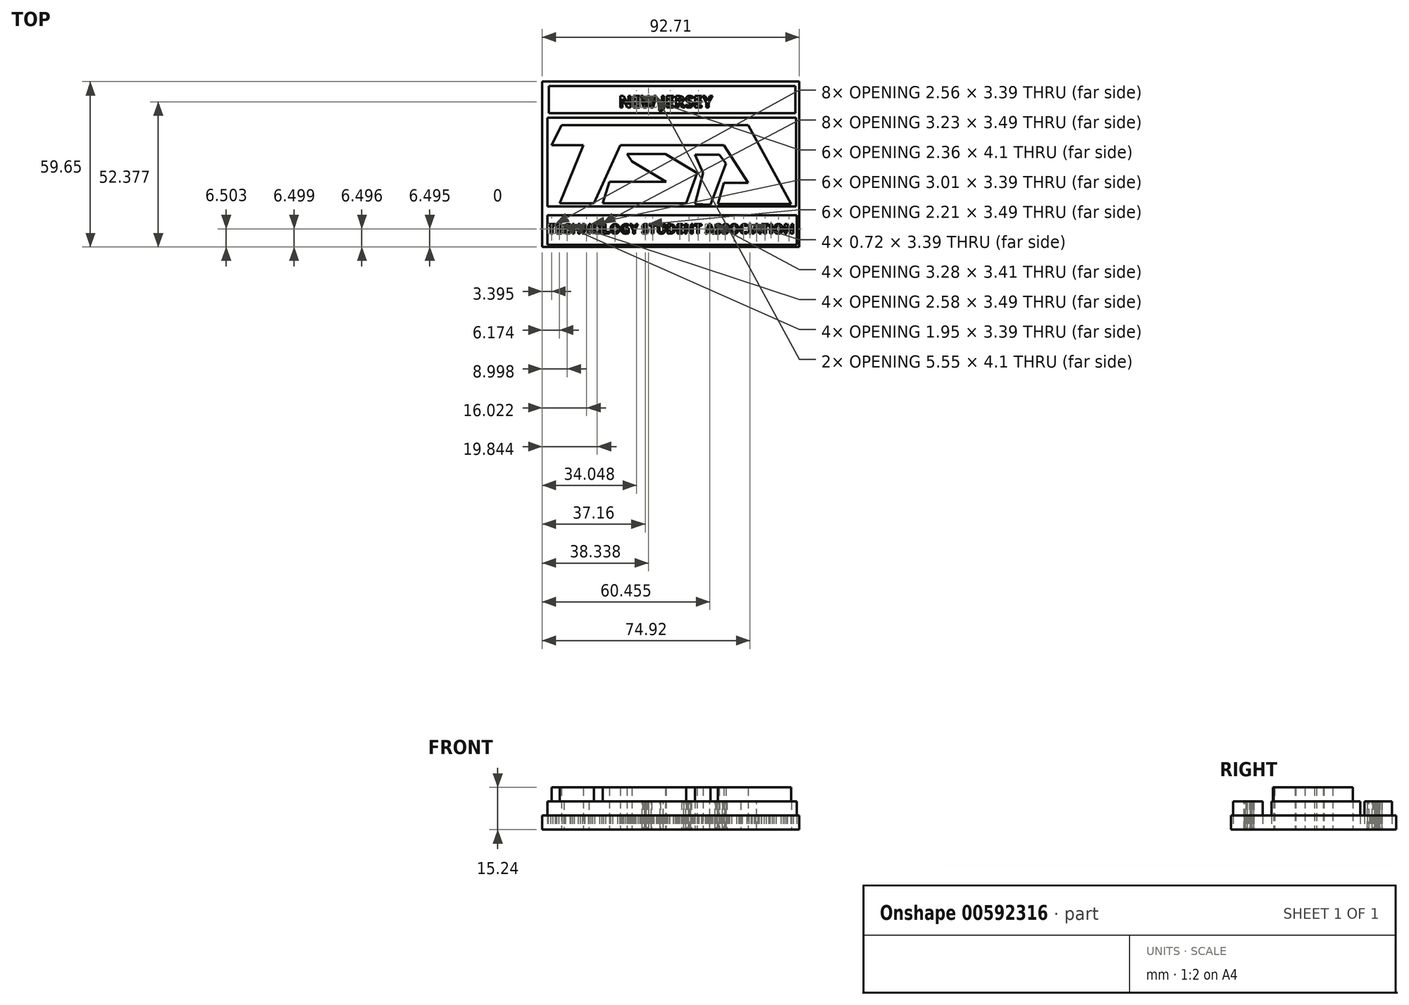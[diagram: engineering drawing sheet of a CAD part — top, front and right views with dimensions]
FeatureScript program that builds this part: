
annotation { "Feature Type Name" : "Feature", "Feature Type Description" : "" }
export const myFeature = defineFeature(function(context is Context, id is Id, definition is map)
    precondition{}
    {
        {
            var Q0;
            Q0=qCreatedBy(makeId("Top.planeOp"),FACE);
            var sketch = newSketch(context, id + "F0", { "sketchPlane" : qUnion([Q0])});
            skLineSegment(sketch, "E0.bottom", {"start": v(-39, -26.63) * mm, "end": v(53.7, -26.63) * mm});
            skLineSegment(sketch, "E0.top", {"start": v(-39, 33.02) * mm, "end": v(53.7, 33.02) * mm});
            skLineSegment(sketch, "E0.left", {"start": v(-39, -26.63) * mm, "end": v(-39, 33.02) * mm});
            skLineSegment(sketch, "E0.right", {"start": v(53.7, -26.63) * mm, "end": v(53.7, 33.02) * mm});
            skSolve(sketch);
        }
        {
            var Q0;
            Q0=makeQuery(id+"F0.imprint","IMPRINT",FACE,{"disambiguationData":[TD([[makeQuery(id+"F0.imprint","IMPRINT",EDGE,{"derivedFrom":sQuery(id+"F0.wireOp",EDGE,"E0.bottom")}),1.0]])]});
            var sketch = newSketch(context, id + "F1", { "sketchPlane" : qUnion([Q0])});
            skLineSegment(sketch, "E1.bottom", {"start": v(-36.61, 21.57) * mm, "end": v(52.32, 21.57) * mm});
            skLineSegment(sketch, "E1.top", {"start": v(-36.61, 31.42) * mm, "end": v(52.32, 31.42) * mm});
            skLineSegment(sketch, "E1.left", {"start": v(-36.61, 21.57) * mm, "end": v(-36.61, 31.42) * mm});
            skLineSegment(sketch, "E1.right", {"start": v(52.32, 21.57) * mm, "end": v(52.32, 31.42) * mm});
            skLineSegment(sketch, "E2.bottom", {"start": v(-37.14, -25.83) * mm, "end": v(52.85, -25.83) * mm});
            skLineSegment(sketch, "E2.top", {"start": v(-37.14, -15.18) * mm, "end": v(52.85, -15.18) * mm});
            skLineSegment(sketch, "E2.left", {"start": v(-37.14, -25.83) * mm, "end": v(-37.14, -15.18) * mm});
            skLineSegment(sketch, "E2.right", {"start": v(52.85, -25.83) * mm, "end": v(52.85, -15.18) * mm});
            skSolve(sketch);
        }
        {
            var Q0;
            Q0=makeQuery(id+"F0.imprint","IMPRINT",FACE,{"disambiguationData":[TD([[makeQuery(id+"F0.imprint","IMPRINT",EDGE,{"derivedFrom":sQuery(id+"F0.wireOp",EDGE,"E0.bottom")}),1.0]])]});
            var sketch = newSketch(context, id + "F2", { "sketchPlane" : qUnion([Q0])});
            skLineSegment(sketch, "E3.bottom", {"start": v(-37.14, -11.98) * mm, "end": v(52.59, -11.98) * mm});
            skLineSegment(sketch, "E3.top", {"start": v(-37.14, 19.97) * mm, "end": v(52.59, 19.97) * mm});
            skLineSegment(sketch, "E3.left", {"start": v(-37.14, -11.98) * mm, "end": v(-37.14, 19.97) * mm});
            skLineSegment(sketch, "E3.right", {"start": v(52.59, -11.98) * mm, "end": v(52.59, 19.97) * mm});
            skSolve(sketch);
        }
        {
            var Q0;
            Q0=makeQuery(id+"F0.imprint","IMPRINT",FACE,{"disambiguationData":[TD([[makeQuery(id+"F0.imprint","IMPRINT",EDGE,{"derivedFrom":sQuery(id+"F0.wireOp",EDGE,"E0.bottom")}),1.0]])]});
            var sketch = newSketch(context, id + "F3", { "sketchPlane" : qUnion([Q0])});
            skLineSegment(sketch, "E4", {"start": v(-32.09, 17.3) * mm, "end": v(35.28, 17.3) * mm});
            skLineSegment(sketch, "E5", {"start": v(35.28, 17.3) * mm, "end": v(50.72, -11.18) * mm});
            skLineSegment(sketch, "E6", {"start": v(50.72, -11.18) * mm, "end": v(24.36, -11.18) * mm});
            skLineSegment(sketch, "E7", {"start": v(24.36, -11.18) * mm, "end": v(26.5, -3.46) * mm});
            skLineSegment(sketch, "E8", {"start": v(26.5, -3.46) * mm, "end": v(35.28, -3.46) * mm});
            skLineSegment(sketch, "E9", {"start": v(35.28, -3.46) * mm, "end": v(26.5, 10.12) * mm});
            skLineSegment(sketch, "E10", {"start": v(26.5, 10.12) * mm, "end": v(-10.78, 10.12) * mm});
            skLineSegment(sketch, "E11", {"start": v(-10.78, 10.12) * mm, "end": v(-20.37, -10.92) * mm});
            skLineSegment(sketch, "E12", {"start": v(-20.37, -10.92) * mm, "end": v(-32.62, -10.92) * mm});
            skLineSegment(sketch, "E13", {"start": v(-32.62, -10.92) * mm, "end": v(-24.1, 10.12) * mm});
            skLineSegment(sketch, "E14", {"start": v(-24.1, 10.12) * mm, "end": v(-35.55, 10.12) * mm});
            skLineSegment(sketch, "E15", {"start": v(-35.55, 10.12) * mm, "end": v(-32.09, 17.3) * mm});
            skLineSegment(sketch, "E16", {"start": v(5.46, 6.92) * mm, "end": v(-8.39, 6.92) * mm});
            skLineSegment(sketch, "E17", {"start": v(-8.39, 6.92) * mm, "end": v(-6.65, 4.24) * mm});
            skLineSegment(sketch, "E18", {"start": v(-6.65, 4.24) * mm, "end": v(5.72, -3.2) * mm});
            skLineSegment(sketch, "E19", {"start": v(5.72, -3.2) * mm, "end": v(-14.78, -3.2) * mm});
            skLineSegment(sketch, "E20", {"start": v(-14.78, -3.2) * mm, "end": v(-17.17, -10.92) * mm});
            skLineSegment(sketch, "E21", {"start": v(-17.17, -10.92) * mm, "end": v(12.91, -10.92) * mm});
            skLineSegment(sketch, "E22", {"start": v(12.91, -10.92) * mm, "end": v(16.9, 0) * mm});
            skLineSegment(sketch, "E23", {"start": v(16.9, 0) * mm, "end": v(5.46, 6.92) * mm});
            skSolve(sketch);
        }
        {
            var Q0;
            Q0 = qSketchRegion(id + "F0", true);
            extrude(context, id + "F4", {"entities" : qUnion([Q0]), "depth" : 5.08 * mm, "offsetDistance" : 25.4 * mm});
        }
        {
            var Q0;
            Q0 = qSketchRegion(id + "F1", true);
            extrude(context, id + "F5", {"entities" : qUnion([Q0]), "depth" : 10.16 * mm, "offsetDistance" : 25.4 * mm});
        }
        {
            var Q0;
            Q0 = qSketchRegion(id + "F2", true);
            extrude(context, id + "F6", {"entities" : qUnion([Q0]), "depth" : 10.16 * mm, "offsetDistance" : 25.4 * mm});
        }
        {
            var Q0;
            Q0 = qSketchRegion(id + "F3", true);
            extrude(context, id + "F7", {"entities" : qUnion([Q0]), "depth" : 15.24 * mm, "offsetDistance" : 25.4 * mm});
        }
        {
            var Q0;
            Q0=qCreatedBy(makeId("Top.planeOp"),FACE);
            var sketch = newSketch(context, id + "F8", { "sketchPlane" : qUnion([Q0])});
            skLineSegment(sketch, "E24", {"start": v(21.7, -11.45) * mm, "end": v(27.28, 3.46) * mm});
            skLineSegment(sketch, "E25", {"start": v(27.28, 3.46) * mm, "end": v(24.9, 6.66) * mm});
            skLineSegment(sketch, "E26", {"start": v(24.9, 6.66) * mm, "end": v(16.1, 6.66) * mm});
            skLineSegment(sketch, "E27", {"start": v(16.1, 6.66) * mm, "end": v(19.04, 0) * mm});
            skLineSegment(sketch, "E28", {"start": v(19.04, 0) * mm, "end": v(16.1, -11.18) * mm});
            skLineSegment(sketch, "E29", {"start": v(16.1, -11.18) * mm, "end": v(21.7, -11.45) * mm});
            skSolve(sketch);
        }
        {
            var Q0;
            Q0 = qSketchRegion(id + "F8", true);
            extrude(context, id + "F9", {"entities" : qUnion([Q0]), "depth" : 15.24 * mm, "offsetDistance" : 25.4 * mm});
        }
        {
            var Q0;
            Q0=qCreatedBy(makeId("Top.planeOp"),FACE);
            var sketch = newSketch(context, id + "F10", { "sketchPlane" : qUnion([Q0])});
            skText(sketch, "E30", { "text": "NEW JERSEY", "fontName": "OpenSans-Bold.ttf"});
            const initialGuessF10  = {"E30": [-0.01132, 0.0237, 1, 0, 0.00413]};
            skSetInitialGuess(sketch, initialGuessF10);
            skSolve(sketch);
        }
        {
            var Q0;
            Q0 = qSketchRegion(id + "F10", true);
            extrude(context, id + "F11", {"entities" : qUnion([Q0]), "depth" : 5.08 * mm, "offsetDistance" : 25.4 * mm});
        }
        {
            var Q0;
            Q0=qCreatedBy(makeId("Top.planeOp"),FACE);
            var sketch = newSketch(context, id + "F12", { "sketchPlane" : qUnion([Q0])});
            skText(sketch, "E31", { "text": "TECHNOLOGY STUDENT ASSOCIATION", "fontName": "OpenSans-Bold.ttf"});
            const initialGuessF12  = {"E31": [-0.03699, -0.02183, 1, 0, 0.00342]};
            skSetInitialGuess(sketch, initialGuessF12);
            skSolve(sketch);
        }
        {
            var Q0;
            Q0 = qSketchRegion(id + "F12", true);
            extrude(context, id + "F13", {"entities" : qUnion([Q0]), "operationType" : NewBodyOperationType.REMOVE, "depth" : 15.24 * mm, "offsetDistance" : 25.4 * mm});
        }
        {
            var Q0;
            Q0 = qSketchRegion(id + "F8", true);
            extrude(context, id + "F14", {"entities" : qUnion([Q0]), "depth" : 15.24 * mm, "offsetDistance" : 25.4 * mm});
        }
        {
            var Q0;
            Q0 = qSketchRegion(id + "F8", true);
            extrude(context, id + "F15", {"entities" : qUnion([Q0]), "depth" : 15.24 * mm, "offsetDistance" : 25.4 * mm});
        }
        {
            var Q0;
            Q0 = qSketchRegion(id + "F12", true);
            extrude(context, id + "F16", {"entities" : qUnion([Q0]), "operationType" : NewBodyOperationType.REMOVE, "endBound" : BoundingType.SYMMETRIC, "depth" : 50.8 * mm, "hasOffset" : true, "offsetDistance" : 25.4 * mm});
        }
        {
            var Q0;
            Q0 = qSketchRegion(id + "F10", true);
            extrude(context, id + "F17", {"entities" : qUnion([Q0]), "operationType" : NewBodyOperationType.REMOVE, "endBound" : BoundingType.SYMMETRIC, "depth" : 23.88 * mm, "offsetDistance" : 25.4 * mm});
        }
    });
